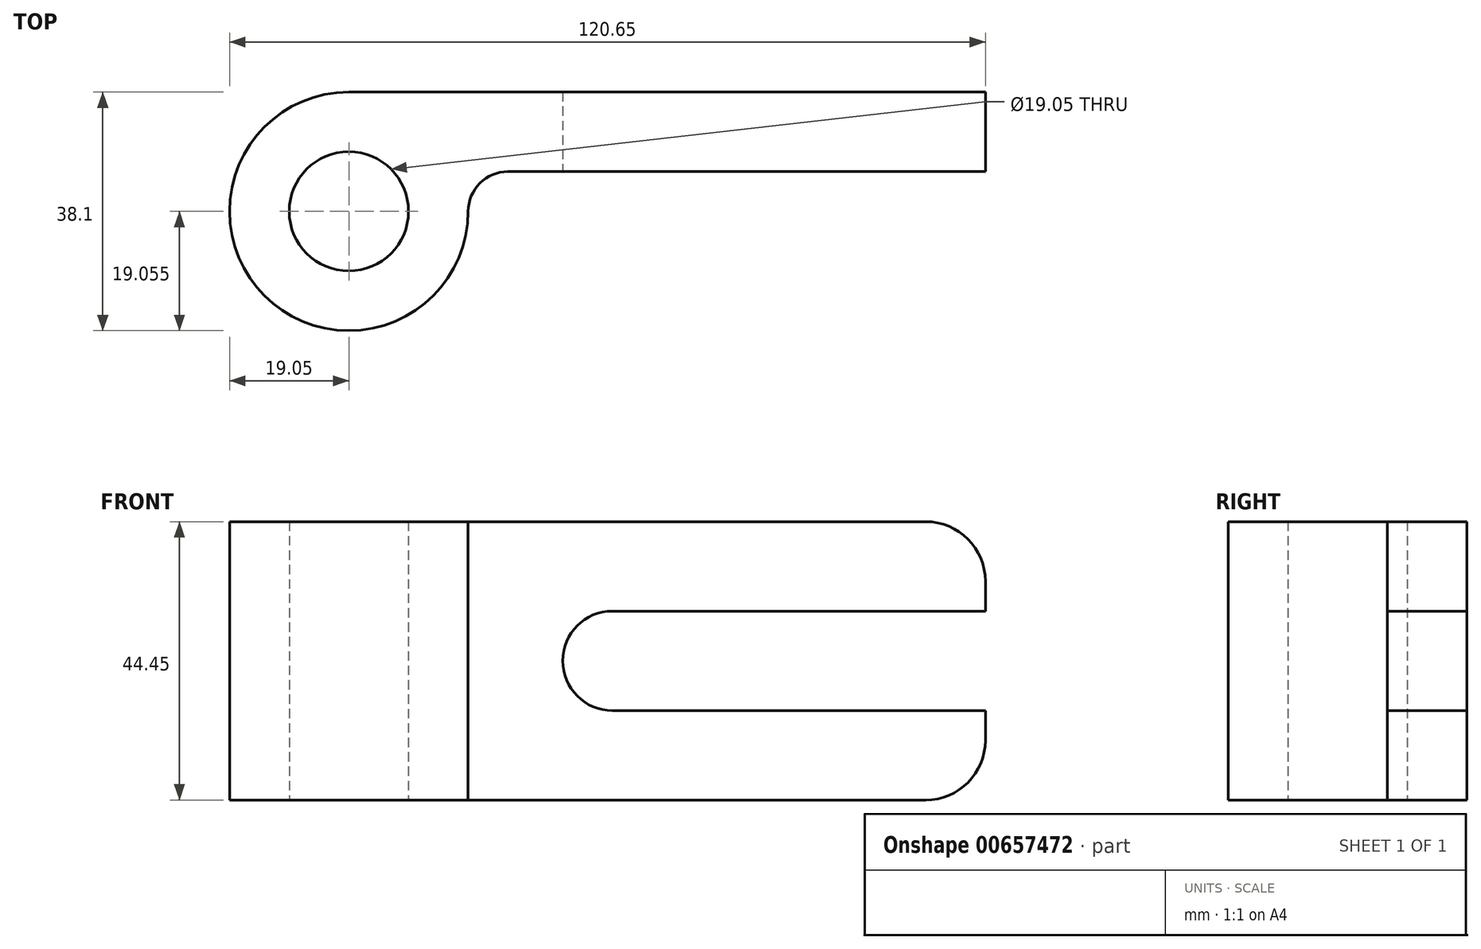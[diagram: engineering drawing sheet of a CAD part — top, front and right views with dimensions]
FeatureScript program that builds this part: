
annotation { "Feature Type Name" : "Feature", "Feature Type Description" : "" }
export const myFeature = defineFeature(function(context is Context, id is Id, definition is map)
    precondition{}
    {
        {
            var Q0;
            Q0=qCreatedBy(makeId("Top.planeOp"),FACE);
            var sketch = newSketch(context, id + "F0", { "sketchPlane" : qUnion([Q0])});
            skLineSegment(sketch, "E0.top", {"start": v(-38.1, 27.9) * mm, "end": v(63.5, 27.9) * mm});
            skArc(sketch, "E1", {"start": v(-38.1, 27.9) * mm, "mid": v(-51.57, -4.62) * mm, "end": v(-19.05, 8.85) * mm});
            skLineSegment(sketch, "E2", {"start": v(63.5, 27.9) * mm, "end": v(63.5, 15.2) * mm});
            skLineSegment(sketch, "E3", {"start": v(63.5, 15.2) * mm, "end": v(0, 15.2) * mm});
            skLineSegment(sketch, "E4", {"start": v(0, 15.2) * mm, "end": v(-12.7, 15.2) * mm});
            skCircle(sketch, "E5", {"center": v(-38.1, 8.85) * mm, "radius": 9.53 * mm});
            skPoint(sketch, "E6.visualSharp", {"position": v(-20.14, 15.2) * mm});
            skArc(sketch, "E6.filletArc", {"start": v(-12.7, 15.2) * mm, "mid": v(-17.2, 13.34) * mm, "end": v(-19.05, 8.85) * mm});
            skLineSegment(sketch, "E7", {"start": v(-38.1, 27.9) * mm, "end": v(-38.1, 27.9) * mm});
            skSolve(sketch);
        }
        {
            var Q0;
            Q0=makeQuery(id+"F0.imprint","IMPRINT",FACE,{"disambiguationData":[TD([[makeQuery(id+"F0.imprint","IMPRINT",EDGE,{"derivedFrom":sQuery(id+"F0.wireOp",EDGE,"E0.top")}),-1.0]])]});
            extrude(context, id + "F1", {"entities" : qUnion([Q0]), "depth" : 44.45 * mm, "offsetDistance" : 25.4 * mm});
        }
        {
            var Q0;
            Q0=makeQuery(id+"F1.opExtrude","SWEPT_FACE",FACE,{"disambiguationData":[OSD([sQuery(id+"F0.wireOp",EDGE,"E3"),sQuery(id+"F0.wireOp",EDGE,"E4")])]});
            var sketch = newSketch(context, id + "F2", { "sketchPlane" : qUnion([Q0])});
            skArc(sketch, "E8", {"start": v(3.97, 30.16) * mm, "mid": v(-3.96, 22.23) * mm, "end": v(3.97, 14.29) * mm});
            skPoint(sketch, "E8.centerSnap0", {"position": v(-12.7, 22.23) * mm});
            skLineSegment(sketch, "E9", {"start": v(3.97, 30.16) * mm, "end": v(63.5, 30.16) * mm});
            skLineSegment(sketch, "E10", {"start": v(3.97, 14.29) * mm, "end": v(63.5, 14.29) * mm});
            skLineSegment(sketch, "E11", {"start": v(63.5, 14.29) * mm, "end": v(63.5, 9.53) * mm});
            skPoint(sketch, "E12.visualSharp", {"position": v(63.5, 0) * mm});
            skArc(sketch, "E12.filletArc", {"start": v(53.98, 0) * mm, "mid": v(60.71, 2.79) * mm, "end": v(63.5, 9.53) * mm});
            skLineSegment(sketch, "E13", {"start": v(63.5, 30.16) * mm, "end": v(63.5, 34.93) * mm});
            skPoint(sketch, "E14.visualSharp", {"position": v(63.5, 44.45) * mm});
            skArc(sketch, "E14.filletArc", {"start": v(63.5, 34.93) * mm, "mid": v(60.71, 41.66) * mm, "end": v(53.97, 44.45) * mm});
            skLineSegment(sketch, "E15", {"start": v(63.5, 44.45) * mm, "end": v(63.5, 34.93) * mm});
            skLineSegment(sketch, "E16", {"start": v(63.5, 0) * mm, "end": v(63.5, 9.53) * mm});
            skLineSegment(sketch, "E17", {"start": v(63.5, 0) * mm, "end": v(53.98, 0) * mm});
            skLineSegment(sketch, "E18", {"start": v(53.97, 44.45) * mm, "end": v(63.5, 44.45) * mm});
            skSolve(sketch);
        }
        {
            var Q0;
            Q0=makeQuery(id+"F2.imprint","IMPRINT",FACE,{"disambiguationData":[TD([[makeQuery(id+"F2.imprint","IMPRINT",EDGE,{"derivedFrom":sQuery(id+"F2.wireOp",EDGE,"E8")}),1.0]])]});
            var Q1;
            Q1=makeQuery(id+"F2.imprint","IMPRINT",FACE,{"disambiguationData":[TD([[makeQuery(id+"F2.imprint","IMPRINT",EDGE,{"derivedFrom":sQuery(id+"F2.wireOp",EDGE,"E14.filletArc")}),-1.0]])]});
            var Q2;
            Q2=makeQuery(id+"F2.imprint","IMPRINT",FACE,{"disambiguationData":[TD([[makeQuery(id+"F2.imprint","IMPRINT",EDGE,{"derivedFrom":sQuery(id+"F2.wireOp",EDGE,"E12.filletArc")}),-1.0]])]});
            extrude(context, id + "F3", {"entities" : qUnion([Q0, Q1, Q2]), "operationType" : NewBodyOperationType.REMOVE, "oppositeDirection" : true, "depth" : 12.7 * mm, "offsetDistance" : 25.4 * mm});
        }
    });
